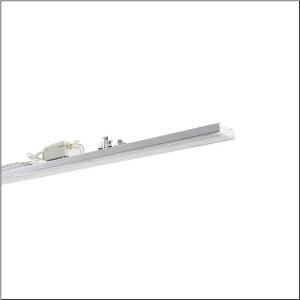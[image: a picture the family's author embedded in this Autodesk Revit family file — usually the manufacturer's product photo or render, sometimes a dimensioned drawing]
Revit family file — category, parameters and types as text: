
# Revit family: licross_11_recessed_ho_51te11dv4lxs
name_source: partatom
category: Lighting Fixtures
units: mm (PartAtom-declared; Revit-internal decimal feet)

## family parameters
Cut with Voids When Loaded = No
Host = Face
Light Source = No
Part Type = Normal
Room Calculation Point = No
Round Connector Dimension = Use Diameter
Shared = No

## types (1)
- --- (1 x LED, 20300 lm, 108 W, 4000K)
    Apparent Load = 108 VA
    CIE Flux Codes = 87 95 99 100 100
    Color Rendering = 80
    Color Temperature = 4000K
    Default Elevation = 1800 mm
    Description = Licross 11 Recessed HO, luminaire insert, of sheet steel, galvanised, coil coated, white, length: 2.250mm, width: 66mm, height: 67mm, LED rated luminous flux: 20.300lm, light colour: 840, SDCM (Standard Deviation of Colour Matching)MacAdam ≤ 2 SDCM (initial), control gear: DALI 2, with plug, 5-pole, with phase selection, mains connection: 220..240V, AC, 50/60Hz, rated input power: 108W, internal wiring halogen-free, primary light control with lens, of plastic, primary optical cover: cover, of PMMA, light emission: direct distribution, primary light characteristic: symmetric, protection rating (complete): IP54, insulation class (complete): insulation class I (protective earthing), certification: CE, ENEC, VDE, UKCA, protection symbol: D if used in an environment with non-conductive dust loads with corresponding accessories, impact resistance: IK06, permissible ambient temperature for indoor applications: -40..+45°C, corresponds to IFS (International Featured Standards) requirements for safety and quality in the food industry, reducing of maximum allowable ambient temperature of 5°C with ceiling mounting, LABS conformity tested according to VDMA 24364:2018-05, The light source and the operating device comply with the requirements of the Ecodesign Regulation (EU) 2019/2020 and are replaceable in accordance with this regulation, packaging unit: 1 piece
    Height = 58 mm
    Lamp = 1 x LED
    Lamp Light Flux = 20300 lm
    Lamp Power = 108 W
    Lamp count = 1
    Length = 2250 mm
    Luminous efficacy = 188 lm/W
    Manufacturer = Siteco
    ModVariant = No
    Model = 51TE11DV4LXS
    Mounting Place = Ceiling
    Mounting Type = Pendant
    Number of Poles = 1
    OnlyDefault = Yes
    Power Factor = 1
    Product Name = Licross 11 Recessed HO
    Product group = luminaire insert | ceiling pendant
    ProductGroupID = 901
    Protection Class = Protection class I
    Protection Degree = IP 54
    RLX_Detail_Level = 1
    RLX_Emergency_Light_Flux = 0 lm
    RLX_Emergency_Type = 0
    RLX_Emergency_Type_DB = No
    RlxData = <blob elided: 29761 chars, md5=8807b05e>
    Socket = socket
    Standby Power = 0 W
    System Light Flux = 20300 lm
    System Power = 108 W
    Type Comments = factory setting: luminous flux: 100 % | dim-lin: 254 | 503 mA
    Type Image = l_1296930.jpg
    URL = http://relux.com
    VarID = @adj_088921
    Voltage = 0 V
    Weight = 0.00 kg
    Width = 66 mm

## geometry (parser evidence)
native form markers: Blend x4, Sweep x8
no freeform markers — native parametric forms only
